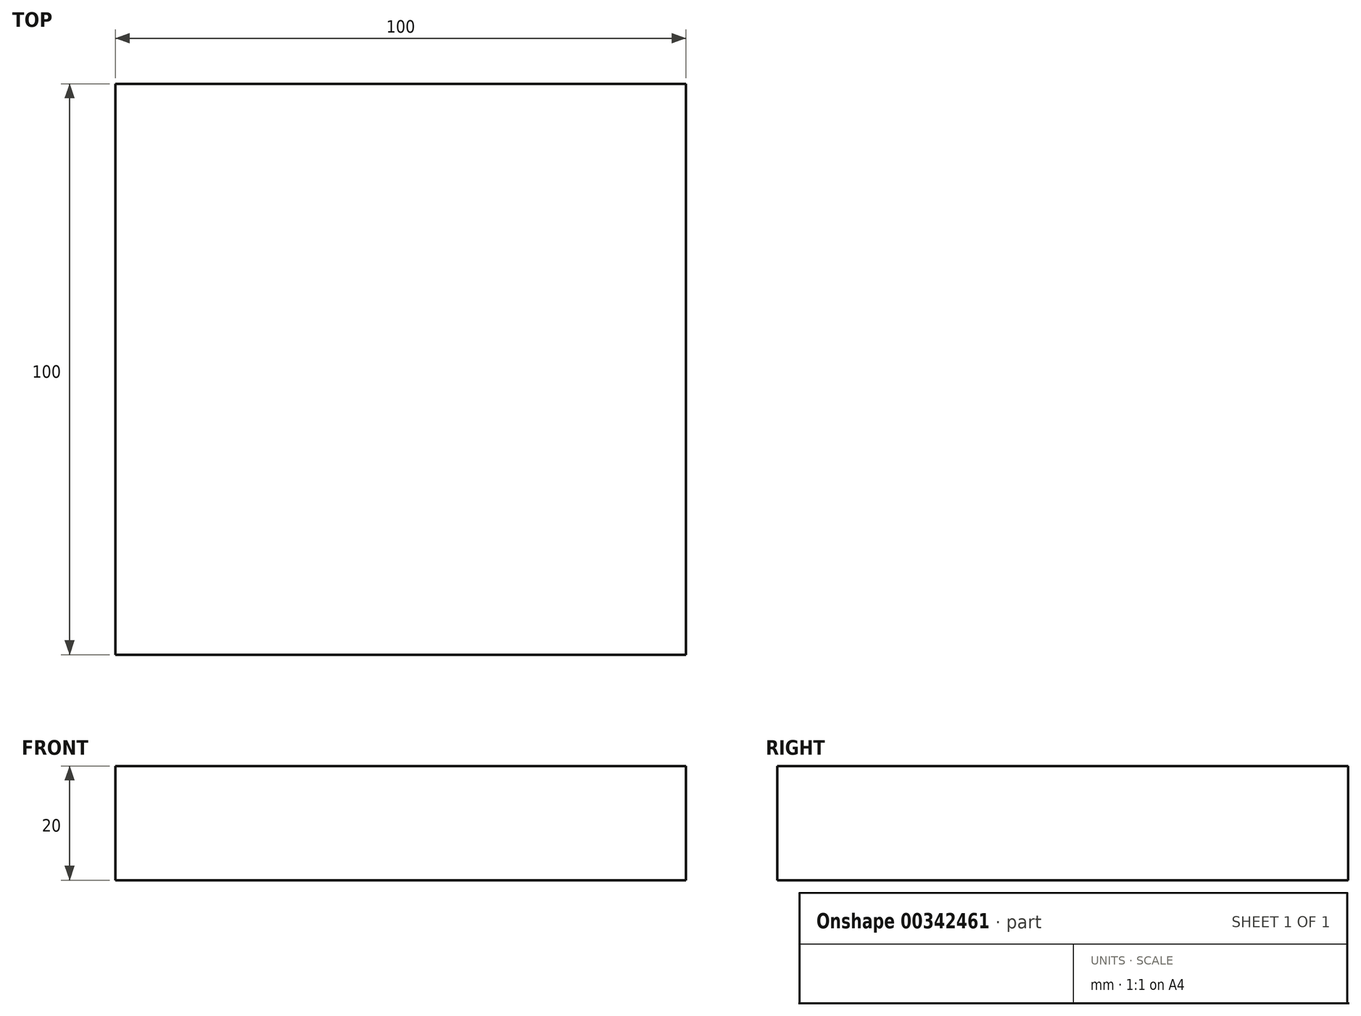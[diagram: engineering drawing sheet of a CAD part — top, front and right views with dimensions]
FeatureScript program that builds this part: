
annotation { "Feature Type Name" : "Feature", "Feature Type Description" : "" }
export const myFeature = defineFeature(function(context is Context, id is Id, definition is map)
    precondition{}
    {
        {
            var Q0;
            Q0=qCreatedBy(makeId("Top.planeOp"),FACE);
            var sketch = newSketch(context, id + "F0", { "sketchPlane" : qUnion([Q0])});
            skLineSegment(sketch, "E0.bottom", {"start": v(50, 50) * mm, "end": v(-50, 50) * mm});
            skLineSegment(sketch, "E0.top", {"start": v(50, -50) * mm, "end": v(-50, -50) * mm});
            skLineSegment(sketch, "E0.left", {"start": v(50, 50) * mm, "end": v(50, -50) * mm});
            skLineSegment(sketch, "E0.right", {"start": v(-50, 50) * mm, "end": v(-50, -50) * mm});
            skPoint(sketch, "E0.middle", {"position": v(0, 0) * mm});
            skSolve(sketch);
        }
        {
            var Q0;
            Q0 = qSketchRegion(id + "F0", true);
            extrude(context, id + "F1", {"entities" : qUnion([Q0]), "depth" : 20 * mm});
        }
    });
